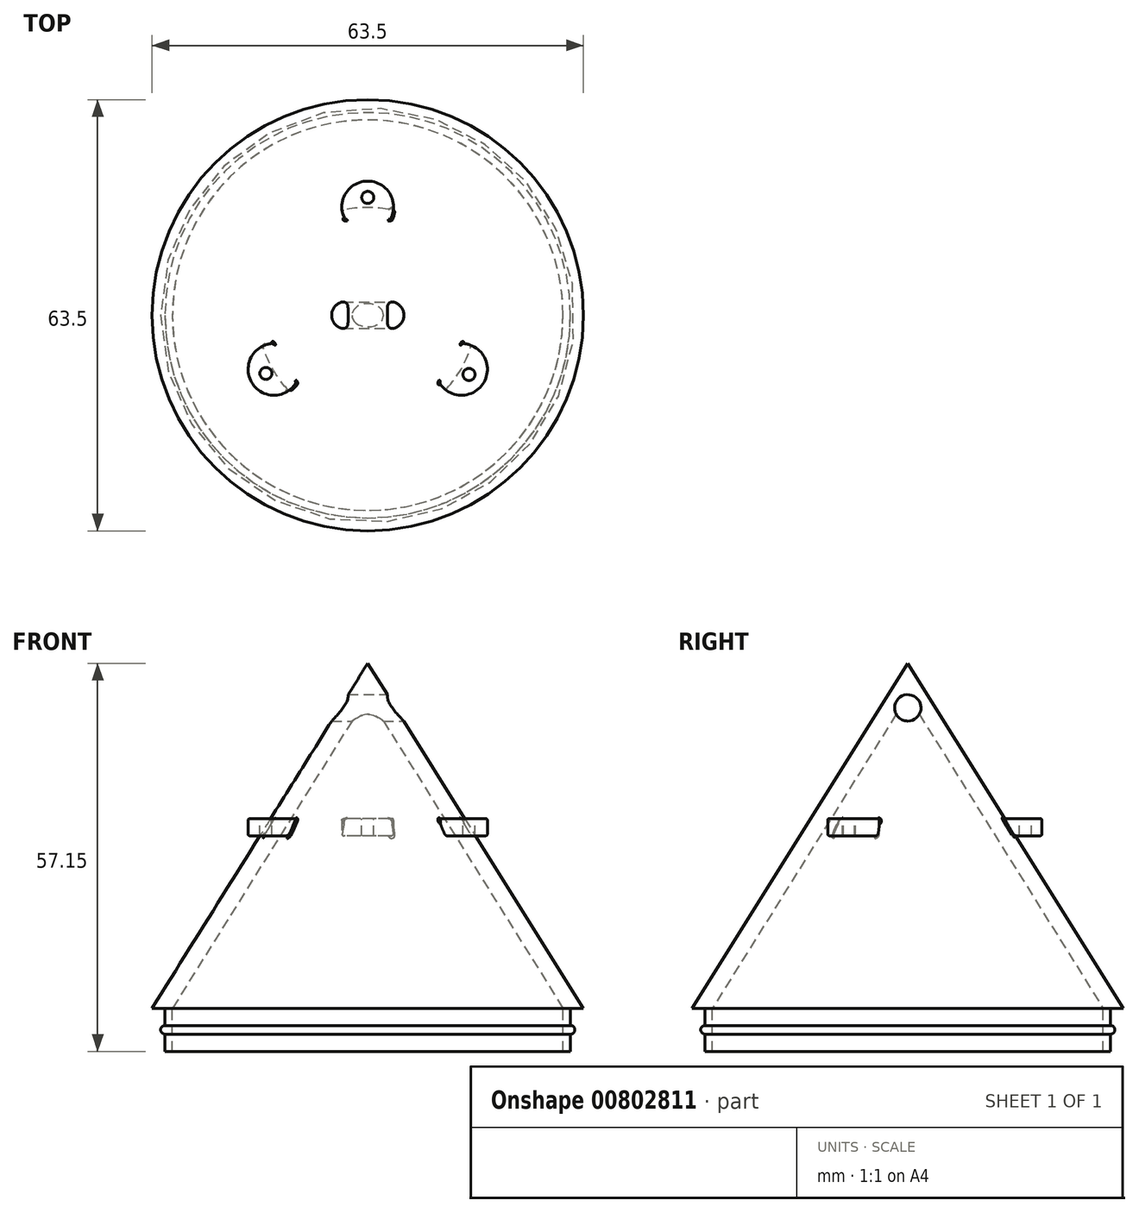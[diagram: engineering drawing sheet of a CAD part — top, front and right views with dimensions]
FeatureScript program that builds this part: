
annotation { "Feature Type Name" : "Feature", "Feature Type Description" : "" }
export const myFeature = defineFeature(function(context is Context, id is Id, definition is map)
    precondition{}
    {
        {
            var Q0;
            Q0=qCreatedBy(makeId("Front.planeOp"),FACE);
            var sketch = newSketch(context, id + "F0", { "sketchPlane" : qUnion([Q0])});
            skLineSegment(sketch, "E0", {"start": v(0, 50.8) * mm, "end": v(31.75, 0) * mm});
            skPoint(sketch, "E1.end.orphan", {"position": v(61.88, 0) * mm});
            skLineSegment(sketch, "E2", {"start": v(0, 0) * mm, "end": v(31.75, 0) * mm});
            skLineSegment(sketch, "E3", {"start": v(0, 50.8) * mm, "end": v(0, 0) * mm});
            skSolve(sketch);
        }
        {
            var Q0;
            Q0=makeQuery(id+"F0.imprint","IMPRINT",FACE,{"disambiguationData":[TD([[makeQuery(id+"F0.imprint","IMPRINT",EDGE,{"derivedFrom":sQuery(id+"F0.wireOp",EDGE,"E0")}),-1.0]])]});
            var Q1;
            Q1=sQuery(id+"F0.wireOp",EDGE,"E3");
            revolve(context, id + "F1", {"surfaceOperationType" : NewSurfaceOperationType.NEW, "entities" : qUnion([Q0]), "axis" : qUnion([Q1]), "revolveType" : RevolveType.FULL});
        }
        {
            var Q0;
            Q0=makeQuery(id+"F1.opRevolve","SWEPT_FACE",FACE,{"disambiguationData":[OSD([sQuery(id+"F0.wireOp",EDGE,"E2")])]});
            shell(context, id + "F2", {"entities" : qUnion([Q0]), "thickness" : 2.54 * mm});
        }
        {
            var Q0;
            Q0=makeQuery(id+"F1.opRevolve","SWEPT_FACE",FACE,{"disambiguationData":[OSD([sQuery(id+"F0.wireOp",EDGE,"E2")])]});
            var sketch = newSketch(context, id + "F3", { "sketchPlane" : qUnion([Q0])});
            skCircle(sketch, "E4", {"center": v(0, 0) * mm, "radius": 29.85 * mm});
            skCircle(sketch, "E5", {"center": v(0, 0) * mm, "radius": 28.58 * mm});
            skSolve(sketch);
        }
        {
            var Q0;
            Q0=makeQuery(id+"F3.imprint","IMPRINT",FACE,{"disambiguationData":[TD([[makeQuery(id+"F3.imprint","IMPRINT",EDGE,{"derivedFrom":sQuery(id+"F3.wireOp",EDGE,"E4")}),1.0]])]});
            extrude(context, id + "F4", {"entities" : qUnion([Q0]), "operationType" : NewBodyOperationType.ADD, "depth" : 6.35 * mm, "offsetDistance" : 25.4 * mm});
        }
        {
            var Q0;
            Q0=makeQuery(id+"F1.opRevolve","SWEPT_FACE",FACE,{"disambiguationData":[OSD([sQuery(id+"F0.wireOp",EDGE,"E2")])]});
            cPlane(context, id + "F5", {"entities" : qUnion([Q0]), "cplaneType" : CPlaneType.OFFSET, "offset" : 3.17 * mm, "width" : 152.4 * mm, "height" : 152.4 * mm});
        }
        {
            var Q0;
            Q0=qCreatedBy(id+"F5.planeOp",FACE);
            var sketch = newSketch(context, id + "F6", { "sketchPlane" : qUnion([Q0])});
            skCircle(sketch, "E6", {"center": v(0, 0) * mm, "radius": 29.85 * mm});
            skSolve(sketch);
        }
        {
            var Q0;
            Q0=qCreatedBy(makeId("Right.planeOp"),FACE);
            var sketch = newSketch(context, id + "F7", { "sketchPlane" : qUnion([Q0])});
            skCircle(sketch, "E7", {"center": v(-29.86, -3.18) * mm, "radius": 0.64 * mm});
            skSolve(sketch);
        }
        {
            var Q0;
            Q0=makeQuery(id+"F7.imprint","IMPRINT",FACE,{"disambiguationData":[TD([[makeQuery(id+"F7.imprint","IMPRINT",EDGE,{"derivedFrom":sQuery(id+"F7.wireOp",EDGE,"E7")}),1.0]])]});
            var Q1;
            Q1=sQuery(id+"F6.wireOp",EDGE,"E6");
            sweep(context, id + "F8", {"operationType" : NewBodyOperationType.ADD, "profiles" : qUnion([Q0]), "path" : qUnion([Q1])});
        }
        {
            var Q0;
            Q0=qCreatedBy(makeId("Right.planeOp"),FACE);
            var sketch = newSketch(context, id + "F9", { "sketchPlane" : qUnion([Q0])});
            skCircle(sketch, "E8", {"center": v(0, 44.24) * mm, "radius": 1.94 * mm});
            skSolve(sketch);
        }
        {
            var Q0;
            Q0=qSketchRegion(id+"F9",true);
            extrude(context, id + "F10", {"entities" : qUnion([Q0]), "operationType" : NewBodyOperationType.REMOVE, "endBound" : BoundingType.THROUGH_ALL, "oppositeDirection" : true, "depth" : 25.4 * mm, "offsetDistance" : 25.4 * mm, "hasSecondDirection" : true, "secondDirectionBound" : SecondDirectionBoundingType.THROUGH_ALL, "secondDirectionOppositeDirection" : false, "secondDirectionDepth" : 25.4 * mm});
        }
        {
            var Q0;
            Q0=qCreatedBy(makeId("Top.planeOp"),FACE);
            cPlane(context, id + "F11", {"entities" : qUnion([Q0]), "cplaneType" : CPlaneType.OFFSET, "offset" : 25.4 * mm, "width" : 152.4 * mm, "height" : 152.4 * mm});
        }
        {
            var Q0;
            Q0=qCreatedBy(makeId("Right.planeOp"),FACE);
            var sketch = newSketch(context, id + "F12", { "sketchPlane" : qUnion([Q0])});
            skLineSegment(sketch, "E9", {"start": v(-15.8, 25.4) * mm, "end": v(15.94, 25.4) * mm});
            skSolve(sketch);
        }
        {
            var Q0;
            Q0=qCreatedBy(id+"F11.planeOp",FACE);
            var sketch = newSketch(context, id + "F13", { "sketchPlane" : qUnion([Q0])});
            skLineSegment(sketch, "E10", {"start": v(0, 15.94) * mm, "end": v(-13.8, -7.97) * mm, "construction": true});
            skLineSegment(sketch, "E11", {"start": v(-13.8, -7.97) * mm, "end": v(13.8, -7.97) * mm, "construction": true});
            skLineSegment(sketch, "E12", {"start": v(13.8, -7.97) * mm, "end": v(0, 15.94) * mm, "construction": true});
            skLineSegment(sketch, "E13.0", {"start": v(0, -15.8) * mm, "end": v(0, 15.94) * mm});
            skArc(sketch, "E14", {"start": v(3.04, 13.64) * mm, "mid": v(0, 19.75) * mm, "end": v(-3.04, 13.64) * mm});
            skArc(sketch, "E15", {"start": v(10.3, -9.45) * mm, "mid": v(17.1, -9.87) * mm, "end": v(13.33, -4.19) * mm});
            skArc(sketch, "E16", {"start": v(-13.33, -4.19) * mm, "mid": v(-17.1, -9.87) * mm, "end": v(-10.3, -9.45) * mm});
            skArc(sketch, "E17", {"start": v(-13.33, -4.19) * mm, "mid": v(-12.1, -6.99) * mm, "end": v(-10.3, -9.45) * mm});
            skArc(sketch, "E18.trimOffspring", {"start": v(3.04, 13.64) * mm, "mid": v(0, 13.97) * mm, "end": v(-3.04, 13.64) * mm});
            skArc(sketch, "E19.trimOffspring", {"start": v(10.3, -9.45) * mm, "mid": v(12.1, -6.99) * mm, "end": v(13.33, -4.19) * mm});
            skSolve(sketch);
        }
        {
            var Q0;
            Q0=makeQuery(id+"F13.imprint","IMPRINT",FACE,{"disambiguationData":[TD([[makeQuery(id+"F13.imprint","IMPRINT",EDGE,{"derivedFrom":sQuery(id+"F13.wireOp",EDGE,"E16")}),1.0]])]});
            var Q1;
            {var subQ0=sQuery(id+"F13.wireOp",EDGE,"E14");Q1=makeQuery(id+"F13.imprint","IMPRINT",FACE,{"disambiguationData":[TD([[makeQuery(id+"F13.imprint","IMPRINT",EDGE,{"derivedFrom":subQ0}),1.0]])]});}
            var Q2;
            Q2=makeQuery(id+"F13.imprint","IMPRINT",FACE,{"disambiguationData":[TD([[makeQuery(id+"F13.imprint","IMPRINT",EDGE,{"derivedFrom":sQuery(id+"F13.wireOp",EDGE,"E15")}),1.0]])]});
            extrude(context, id + "F14", {"entities" : qUnion([Q0, Q1, Q2]), "operationType" : NewBodyOperationType.ADD, "depth" : 2.54 * mm, "offsetDistance" : 25.4 * mm});
        }
        {
            var Q0;
            Q0=makeQuery(id+"F14.opExtrude","CAP_FACE",FACE,{"disambiguationData":[OSD([sQuery(id+"F13.wireOp",EDGE,"E15"),sQuery(id+"F13.wireOp",EDGE,"E19.trimOffspring")])],"isStart":false});
            cPlane(context, id + "F15", {"entities" : qUnion([Q0]), "cplaneType" : CPlaneType.OFFSET, "offset" : 0 * mm, "width" : 152.4 * mm, "height" : 152.4 * mm});
        }
        {
            var Q0;
            Q0=qCreatedBy(id+"F15.planeOp",FACE);
            var sketch = newSketch(context, id + "F16", { "sketchPlane" : qUnion([Q0])});
            skCircle(sketch, "E20", {"center": v(0, 17.34) * mm, "radius": 0.89 * mm});
            skCircle(sketch, "E21", {"center": v(14.9, -8.72) * mm, "radius": 0.89 * mm});
            skCircle(sketch, "E22", {"center": v(-15, -8.58) * mm, "radius": 0.89 * mm});
            skSolve(sketch);
        }
        {
            var Q0;
            Q0=qSketchRegion(id+"F16",true);
            extrude(context, id + "F17", {"entities" : qUnion([Q0]), "operationType" : NewBodyOperationType.REMOVE, "endBound" : BoundingType.UP_TO_NEXT, "oppositeDirection" : true, "depth" : 1.27 * mm, "offsetDistance" : 25.4 * mm});
        }
        {
            var Q0;
            Q0=makeQuery(id+"F14.boolean.opBoolean","INTERSECT",EDGE,{"derivedFrom":[makeQuery(id+"F1.opRevolve","SWEPT_FACE",FACE,{"disambiguationData":[OSD([sQuery(id+"F0.wireOp",EDGE,"E0")])]}),makeQuery(id+"F14.opExtrude","CAP_FACE",FACE,{"disambiguationData":[OSD([sQuery(id+"F13.wireOp",EDGE,"E16"),sQuery(id+"F13.wireOp",EDGE,"E17")])],"isStart":true})]});
            var Q1;
            Q1=makeQuery(id+"F14.boolean.opBoolean","INTERSECT",EDGE,{"disambiguationData":[OD(1.0)],"derivedFrom":[makeQuery(id+"F1.opRevolve","SWEPT_FACE",FACE,{"disambiguationData":[OSD([sQuery(id+"F0.wireOp",EDGE,"E0")])]}),makeQuery(id+"F14.opExtrude","SWEPT_FACE",FACE,{"disambiguationData":[OSD([sQuery(id+"F13.wireOp",EDGE,"E16")])]})]});
            var Q2;
            Q2=makeQuery(id+"F14.boolean.opBoolean","INTERSECT",EDGE,{"derivedFrom":[makeQuery(id+"F1.opRevolve","SWEPT_FACE",FACE,{"disambiguationData":[OSD([sQuery(id+"F0.wireOp",EDGE,"E0")])]}),makeQuery(id+"F14.opExtrude","CAP_FACE",FACE,{"disambiguationData":[OSD([sQuery(id+"F13.wireOp",EDGE,"E16"),sQuery(id+"F13.wireOp",EDGE,"E17")])],"isStart":false})]});
            var Q3;
            Q3=makeQuery(id+"F14.opExtrude","CAP_EDGE",EDGE,{"disambiguationData":[OSD([sQuery(id+"F13.wireOp",EDGE,"E16")])],"isStart":false});
            var Q4;
            Q4=makeQuery(id+"F14.opExtrude","CAP_EDGE",EDGE,{"disambiguationData":[OSD([sQuery(id+"F13.wireOp",EDGE,"E16")])],"isStart":true});
            var Q5;
            Q5=makeQuery(id+"F14.opExtrude","CAP_EDGE",EDGE,{"disambiguationData":[OSD([sQuery(id+"F13.wireOp",EDGE,"E15")])],"isStart":false});
            var Q6;
            Q6=makeQuery(id+"F14.opExtrude","CAP_EDGE",EDGE,{"disambiguationData":[OSD([sQuery(id+"F13.wireOp",EDGE,"E15")])],"isStart":true});
            var Q7;
            Q7=makeQuery(id+"F14.boolean.opBoolean","INTERSECT",EDGE,{"derivedFrom":[makeQuery(id+"F1.opRevolve","SWEPT_FACE",FACE,{"disambiguationData":[OSD([sQuery(id+"F0.wireOp",EDGE,"E0")])]}),makeQuery(id+"F14.opExtrude","CAP_FACE",FACE,{"disambiguationData":[OSD([sQuery(id+"F13.wireOp",EDGE,"E15"),sQuery(id+"F13.wireOp",EDGE,"E19.trimOffspring")])],"isStart":false})]});
            var Q8;
            Q8=makeQuery(id+"F14.boolean.opBoolean","INTERSECT",EDGE,{"derivedFrom":[makeQuery(id+"F1.opRevolve","SWEPT_FACE",FACE,{"disambiguationData":[OSD([sQuery(id+"F0.wireOp",EDGE,"E0")])]}),makeQuery(id+"F14.opExtrude","CAP_FACE",FACE,{"disambiguationData":[OSD([sQuery(id+"F13.wireOp",EDGE,"E14"),sQuery(id+"F13.wireOp",EDGE,"E18.trimOffspring")])],"isStart":false})]});
            var Q9;
            Q9=makeQuery(id+"F14.boolean.opBoolean","INTERSECT",EDGE,{"disambiguationData":[OD(1.0)],"derivedFrom":[makeQuery(id+"F1.opRevolve","SWEPT_FACE",FACE,{"disambiguationData":[OSD([sQuery(id+"F0.wireOp",EDGE,"E0")])]}),makeQuery(id+"F14.opExtrude","SWEPT_FACE",FACE,{"disambiguationData":[OSD([sQuery(id+"F13.wireOp",EDGE,"E14")])]})]});
            var Q10;
            Q10=makeQuery(id+"F14.opExtrude","CAP_EDGE",EDGE,{"disambiguationData":[OSD([sQuery(id+"F13.wireOp",EDGE,"E14")])],"isStart":false});
            var Q11;
            Q11=makeQuery(id+"F14.opExtrude","CAP_EDGE",EDGE,{"disambiguationData":[OSD([sQuery(id+"F13.wireOp",EDGE,"E14")])],"isStart":true});
            var Q12;
            Q12=makeQuery(id+"F17.boolean.opBoolean","COPY",EDGE,{"derivedFrom":makeQuery(id+"F17.opExtrude","CAP_EDGE",EDGE,{"disambiguationData":[OSD([sQuery(id+"F16.wireOp",EDGE,"E20")])],"isStart":true})});
            var Q13;
            Q13=makeQuery(id+"F17.boolean.opBoolean","COPY",EDGE,{"derivedFrom":makeQuery(id+"F17.opExtrude","CAP_EDGE",EDGE,{"disambiguationData":[OSD([sQuery(id+"F16.wireOp",EDGE,"E22")])],"isStart":true})});
            var Q14;
            Q14=makeQuery(id+"F17.boolean.opBoolean","COPY",EDGE,{"derivedFrom":makeQuery(id+"F17.opExtrude","CAP_EDGE",EDGE,{"disambiguationData":[OSD([sQuery(id+"F16.wireOp",EDGE,"E21")])],"isStart":true})});
            fillet(context, id + "F18", {"entities" : qUnion([Q0, Q1, Q2, Q3, Q4, Q5, Q6, Q7, Q8, Q9, Q10, Q11, Q12, Q13, Q14]), "radius" : 0.25 * mm, "tangentPropagation" : true, "allowEdgeOverflow" : false});
        }
    });
